# Revit family: 306_457fd781672c437d90456a1f4e4ea4
name_source: partatom
category: Pipe Accessories
revit_build: Autodesk Revit 2018 (Build: 20170223_1515(x64)
units: mm (PartAtom-declared; Revit-internal decimal feet)

## family parameters
Always vertical = Yes
Cut with Voids When Loaded = No
Part Type = Valve - Breaks Into
Round Connector Dimension = Use Diameter
Shared = No
Work Plane-Based = No

## types (3) — shared parameters
CenSd_DB2_6 = 8 mm  [stored 0.0262467 ft]
D17 = 38 mm
DB = 10 mm  [stored 0.0328084 ft]
DB1 = 12 mm  [stored 0.0393701 ft]
DB2 = 9 mm  [stored 0.0295276 ft]
Description = Backflow preventer BA 6600
H14 = 9 mm  [stored 0.0295276 ft]
H16 = 21 mm
H16__ve = -21 mm
L2D_Min = 3048 mm
L4 = 2 mm  [stored 0.00656168 ft]
L7 = 32 mm
Manufacturer = SYR
QmdConnectorList = 301;D;302;D
magiPartTypeId = 306
magiProductFamilyId = 457fd781672c437d90456a1f4e4ea4

## per-type parameters (varying)
- SYR-BA-6600-100: CenSd_D10_6=27 mm; D=100 mm; D10=31 mm; D11=83 mm; D12=79 mm; D13=74 mm; D14=61 mm; D15=53 mm; D16=44 mm; D18=53 mm; D19=75 mm; D4=110 mm; D4__ve=-110 mm  [stored -0.360892 ft]; D5=55 mm; D6=61 mm; D7=88 mm; D8=66 mm; D9=93 mm; H10=47 mm; H10__ve=-47 mm; H11=16 mm; H12=95 mm; H12__ve=-95 mm; H13=38 mm; H13__ve=-38 mm; H2=66 mm; H3=132 mm; H3__ve=-132 mm  [stored -0.433071 ft]; H5=11 mm; H6=22 mm  [stored 0.0721785 ft]; H7=11 mm; H8=34 mm; H9=32 mm; H9__ve=-32 mm; L1=175 mm; L2=33 mm; L2D=350 mm; L3=18 mm; L3__ve=-18 mm; L5=7 mm  [stored 0.0229659 ft]; L5__ve=-7 mm; L6=68 mm; L6__ve=-68 mm; L8=37 mm; L9=45 mm; W2D=100 mm; ZX=110 mm; magiProductId=bb336a09341f41649f218b57a13670
- SYR-BA-6600-80: CenSd_D10_6=27 mm; D=80 mm; D10=31 mm; D11=83 mm; D12=79 mm; D13=74 mm; D14=61 mm; D15=53 mm; D16=44 mm; D18=43 mm; D19=65 mm; D4=100 mm; D4__ve=-100 mm  [stored -0.328084 ft]; D5=50 mm; D6=55 mm; D7=88 mm; D8=60 mm; D9=93 mm; H10=47 mm; H10__ve=-47 mm; H11=16 mm; H12=93 mm; H12__ve=-93 mm; H13=37 mm; H13__ve=-37 mm; H2=60 mm; H3=120 mm; H3__ve=-120 mm; H5=10 mm  [stored 0.0328084 ft]; H6=20 mm  [stored 0.0656168 ft]; H7=11 mm; H8=33 mm; H9=31 mm; H9__ve=-31 mm; L1=175 mm; L2=33 mm; L2D=350 mm; L3=18 mm; L3__ve=-18 mm; L5=7 mm  [stored 0.0229659 ft]; L5__ve=-7 mm; L6=68 mm; L6__ve=-68 mm; L8=37 mm; L9=45 mm; W2D=80 mm; ZX=100 mm; magiProductId=46d9ffa5bb0d4e1690d7c4dd5135bb
- SYR-BA-6600-65: CenSd_D10_6=25 mm  [stored 0.082021 ft]; D=65 mm; D10=29 mm; D11=78 mm; D12=74 mm; D13=70 mm; D14=58 mm; D15=50 mm; D16=41 mm; D18=36 mm; D19=58 mm; D4=93 mm; D4__ve=-93 mm; D5=46 mm; D6=51 mm; D7=83 mm; D8=56 mm; D9=88 mm; H10=46 mm; H10__ve=-46 mm; H11=15 mm  [stored 0.0492126 ft]; H12=93 mm; H12__ve=-93 mm; H13=37 mm; H13__ve=-37 mm; H2=56 mm; H3=111 mm; H3__ve=-111 mm; H5=9 mm  [stored 0.0295276 ft]; H6=18 mm; H7=10 mm  [stored 0.0328084 ft]; H8=29 mm; H9=31 mm; H9__ve=-31 mm; L1=165 mm; L2=31 mm; L2D=330 mm; L3=17 mm; L3__ve=-17 mm; L5=6 mm  [stored 0.019685 ft]; L5__ve=-6 mm; L6=64 mm; L6__ve=-64 mm; L8=36 mm; L9=43 mm; W2D=65 mm; ZX=93 mm; magiProductId=9b3d18a465564e8cbb558a7127c424

note: column(s) folded — value = type name in every type: MC Product Code

note: [stored X ft] marks values corroborated as IEEE doubles in the binary element streams (Revit-internal decimal feet)

## geometry (parser evidence)
native form markers: Sweep x2
no freeform markers — native parametric forms only
